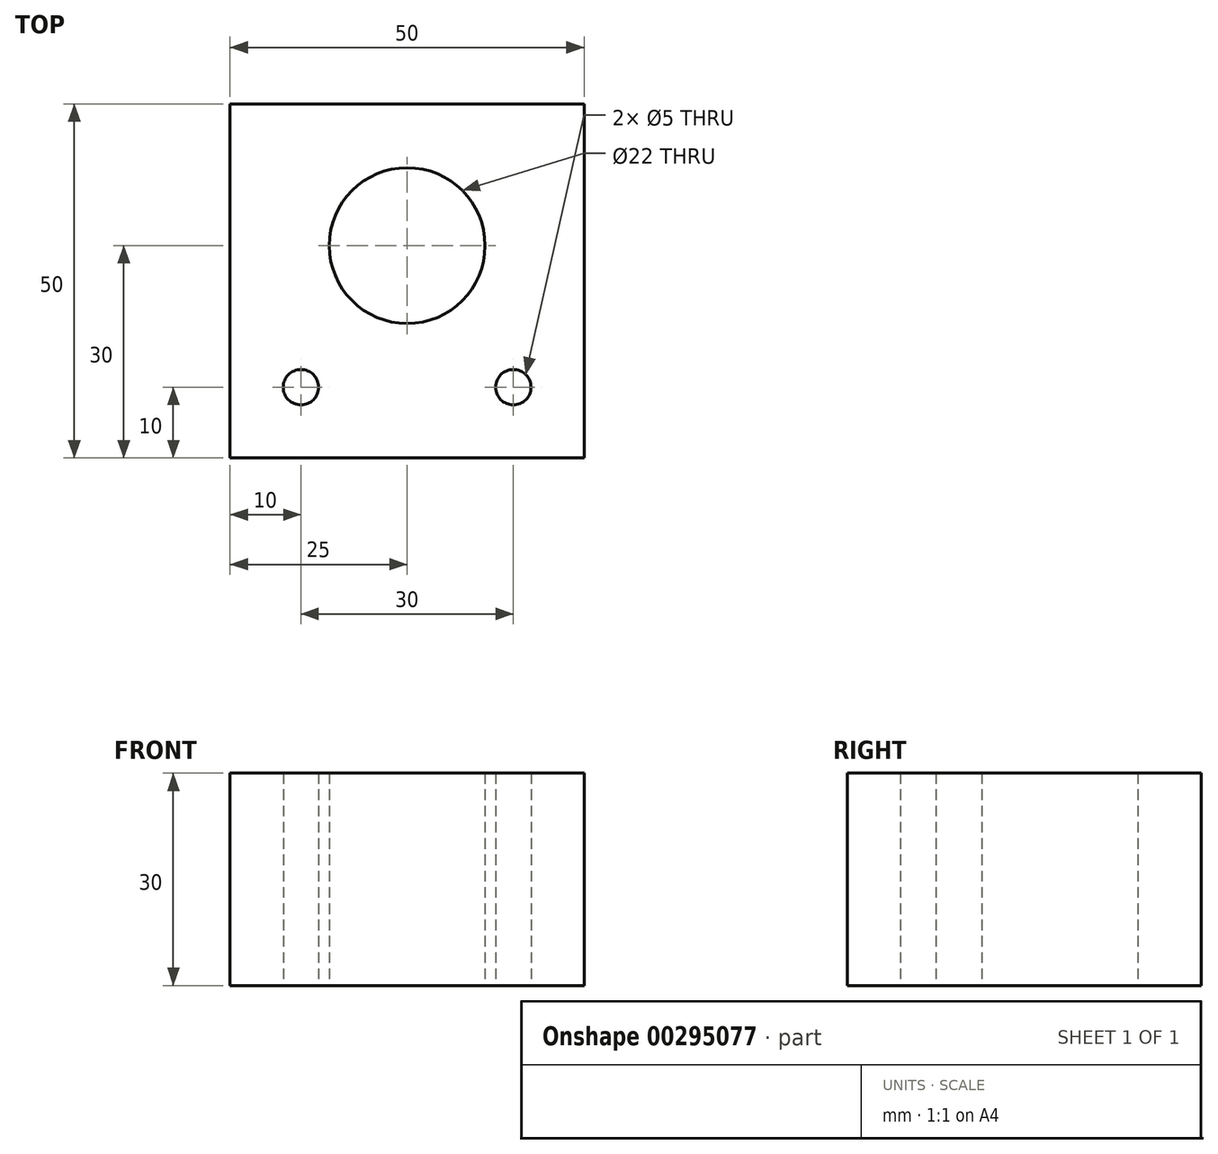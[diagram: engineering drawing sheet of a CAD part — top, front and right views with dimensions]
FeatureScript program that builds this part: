
annotation { "Feature Type Name" : "Feature", "Feature Type Description" : "" }
export const myFeature = defineFeature(function(context is Context, id is Id, definition is map)
    precondition{}
    {
        {
            var Q0;
            Q0=qCreatedBy(makeId("Top.planeOp"),FACE);
            var sketch = newSketch(context, id + "F0", { "sketchPlane" : qUnion([Q0])});
            skLineSegment(sketch, "E0.bottom", {"start": v(25, 25) * mm, "end": v(-25, 25) * mm});
            skLineSegment(sketch, "E0.top", {"start": v(25, -25) * mm, "end": v(-25, -25) * mm});
            skLineSegment(sketch, "E0.left", {"start": v(25, 25) * mm, "end": v(25, -25) * mm});
            skLineSegment(sketch, "E0.right", {"start": v(-25, 25) * mm, "end": v(-25, -25) * mm});
            skPoint(sketch, "E0.middle", {"position": v(0, 0) * mm});
            skCircle(sketch, "E1", {"center": v(0, 5) * mm, "radius": 11 * mm});
            skCircle(sketch, "E2", {"center": v(15, -15) * mm, "radius": 2.5 * mm});
            skCircle(sketch, "E3", {"center": v(-15, -15) * mm, "radius": 2.5 * mm});
            skSolve(sketch);
        }
        {
            var Q0;
            Q0 = qSketchRegion(id + "F0", true);
            extrude(context, id + "F1", {"entities" : qUnion([Q0]), "depth" : 30 * mm});
        }
    });
